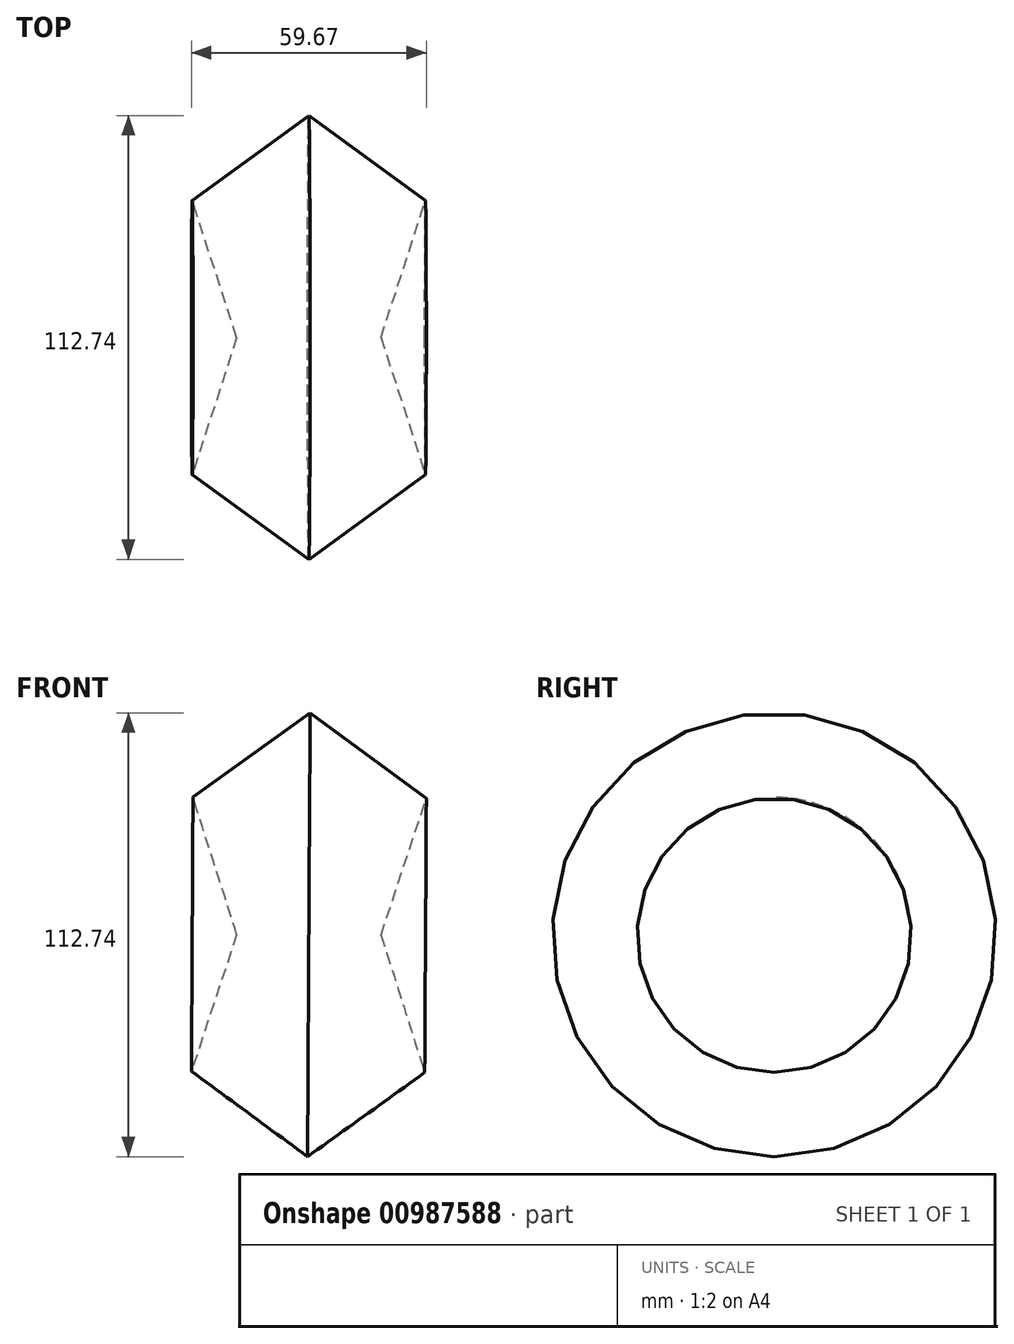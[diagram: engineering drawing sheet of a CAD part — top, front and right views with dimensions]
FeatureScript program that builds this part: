
annotation { "Feature Type Name" : "Feature", "Feature Type Description" : "" }
export const myFeature = defineFeature(function(context is Context, id is Id, definition is map)
    precondition{}
    {
        {
            var Q0;
            Q0=qCreatedBy(makeId("Front.planeOp"),FACE);
            var sketch = newSketch(context, id + "F0", { "sketchPlane" : qUnion([Q0])});
            skCircle(sketch, "E0.cCircle", {"center": v(0, 0) * mm, "radius": 25.21 * mm, "construction": true});
            skLineSegment(sketch, "E0.0", {"start": v(-18.46, -25.1) * mm, "end": v(-29.58, 9.8) * mm});
            skLineSegment(sketch, "E0.1", {"start": v(-29.58, 9.8) * mm, "end": v(0.18, 31.16) * mm});
            skLineSegment(sketch, "E0.2", {"start": v(0.18, 31.16) * mm, "end": v(29.7, 9.46) * mm});
            skLineSegment(sketch, "E0.3", {"start": v(29.7, 9.46) * mm, "end": v(18.17, -25.32) * mm});
            skLineSegment(sketch, "E0.4", {"start": v(18.17, -25.32) * mm, "end": v(-18.46, -25.1) * mm});
            skPoint(sketch, "E0.0.midPoint", {"position": v(-24.02, -7.65) * mm});
            skSolve(sketch);
        }
        {
            var Q0;
            Q0=makeQuery(id+"F0.imprint","IMPRINT",FACE,{"disambiguationData":[TD([[makeQuery(id+"F0.imprint","IMPRINT",EDGE,{"derivedFrom":sQuery(id+"F0.wireOp",EDGE,"E0.0")}),-1.0]])]});
            var Q1;
            Q1=sQuery(id+"F0.wireOp",EDGE,"E0.4");
            revolve(context, id + "F1", {"surfaceOperationType" : NewSurfaceOperationType.NEW, "entities" : qUnion([Q0]), "axis" : qUnion([Q1]), "revolveType" : RevolveType.FULL});
        }
    });
